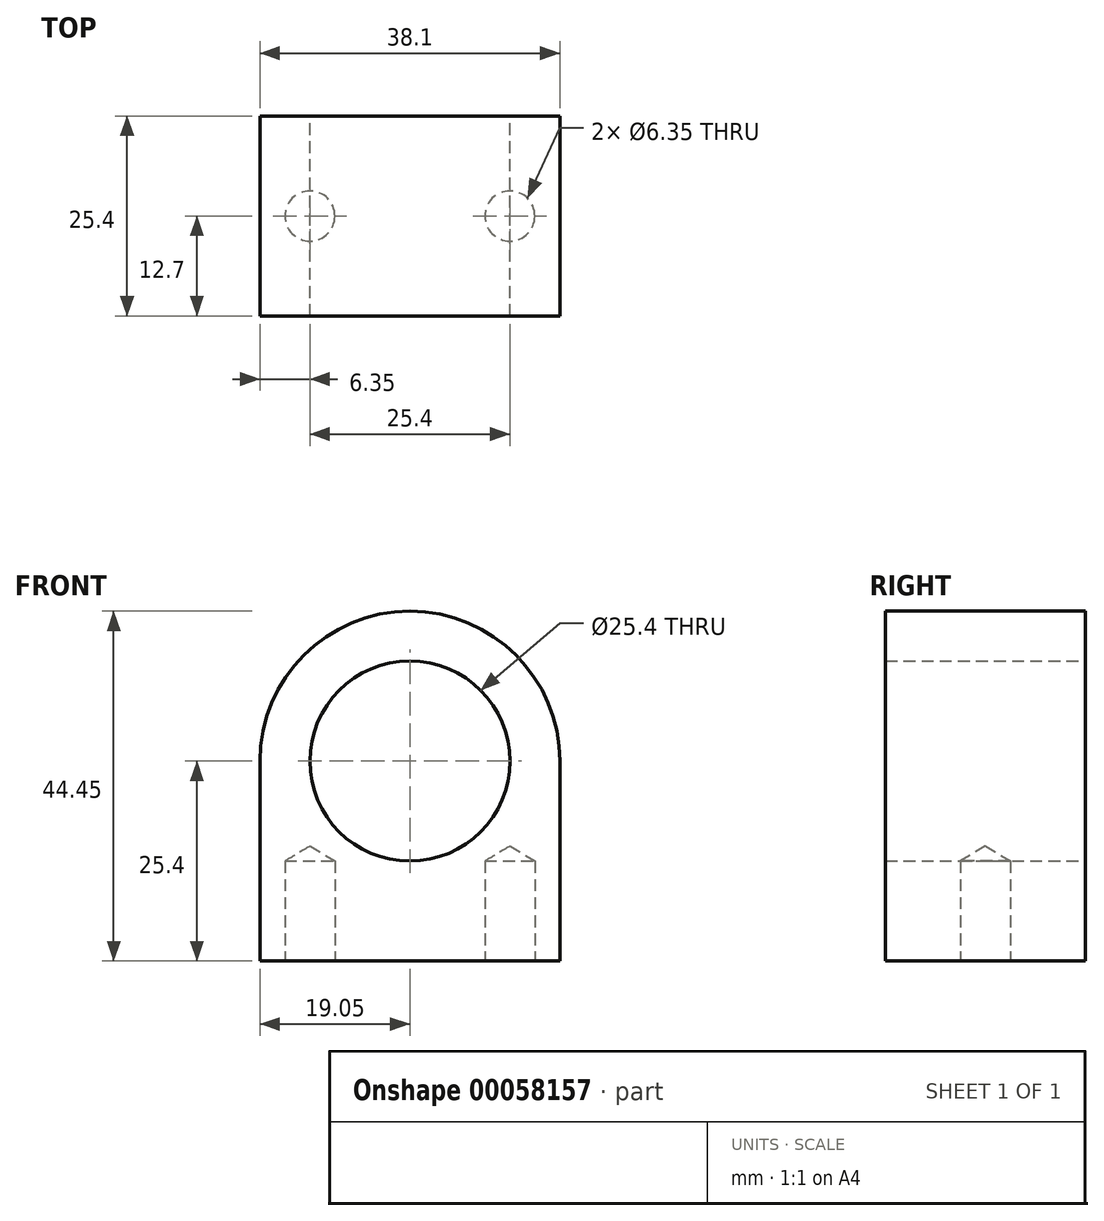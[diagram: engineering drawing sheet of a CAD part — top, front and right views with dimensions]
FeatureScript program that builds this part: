
annotation { "Feature Type Name" : "Feature", "Feature Type Description" : "" }
export const myFeature = defineFeature(function(context is Context, id is Id, definition is map)
    precondition{}
    {
        {
            var Q0;
            Q0=qCreatedBy(makeId("Front.planeOp"),FACE);
            var sketch = newSketch(context, id + "F0", { "sketchPlane" : qUnion([Q0])});
            skArc(sketch, "E0", {"start": v(19.05, 0) * mm, "mid": v(0, 19.05) * mm, "end": v(-19.05, 0) * mm});
            skLineSegment(sketch, "E1", {"start": v(-19.05, 0) * mm, "end": v(-19.05, -25.4) * mm});
            skLineSegment(sketch, "E2", {"start": v(-19.05, -25.4) * mm, "end": v(19.05, -25.4) * mm});
            skLineSegment(sketch, "E3", {"start": v(19.05, -25.4) * mm, "end": v(19.05, 0) * mm});
            skCircle(sketch, "E4", {"center": v(0, 0) * mm, "radius": 12.7 * mm});
            skSolve(sketch);
        }
        {
            var Q0;
            Q0 = qSketchRegion(id + "F0", true);
            extrude(context, id + "F1", {"entities" : qUnion([Q0]), "endBound" : BoundingType.SYMMETRIC, "depth" : 25.4 * mm});
        }
        {
            var Q0;
            Q0=makeQuery(id+"F1.opExtrude","SWEPT_FACE",FACE,{"disambiguationData":[OSD([sQuery(id+"F0.wireOp",EDGE,"E2")])]});
            var sketch = newSketch(context, id + "F2", { "sketchPlane" : qUnion([Q0])});
            skCircle(sketch, "E5", {"center": v(-12.7, 0) * mm, "radius": 3.18 * mm});
            skCircle(sketch, "E6", {"center": v(12.7, 0) * mm, "radius": 3.18 * mm});
            skSolve(sketch);
        }
        {
            var Q0;
            Q0=sQuery(id+"F2.wireOp",VERTEX,"E5.center");
            var Q1;
            Q1=sQuery(id+"F2.wireOp",VERTEX,"E6.center");
            var Q2;
            Q2=makeQuery(id+"F1.opExtrude","SWEPT_BODY",BODY,{"disambiguationData":[OSD([sQuery(id+"F0.wireOp",EDGE,"E0"),sQuery(id+"F0.wireOp",EDGE,"E1"),sQuery(id+"F0.wireOp",EDGE,"E2"),sQuery(id+"F0.wireOp",EDGE,"E3"),sQuery(id+"F0.wireOp",EDGE,"E4")])]});
            hole(context, id + "F3", {"style" : HoleStyle.SIMPLE, "holeDiameter" : 6.35 * mm, "endStyle" : HoleEndStyle.BLIND, "holeDepth" : 12.7 * mm, "locations" : qUnion([Q0, Q1]), "scope" : qUnion([Q2])});
        }
    });
